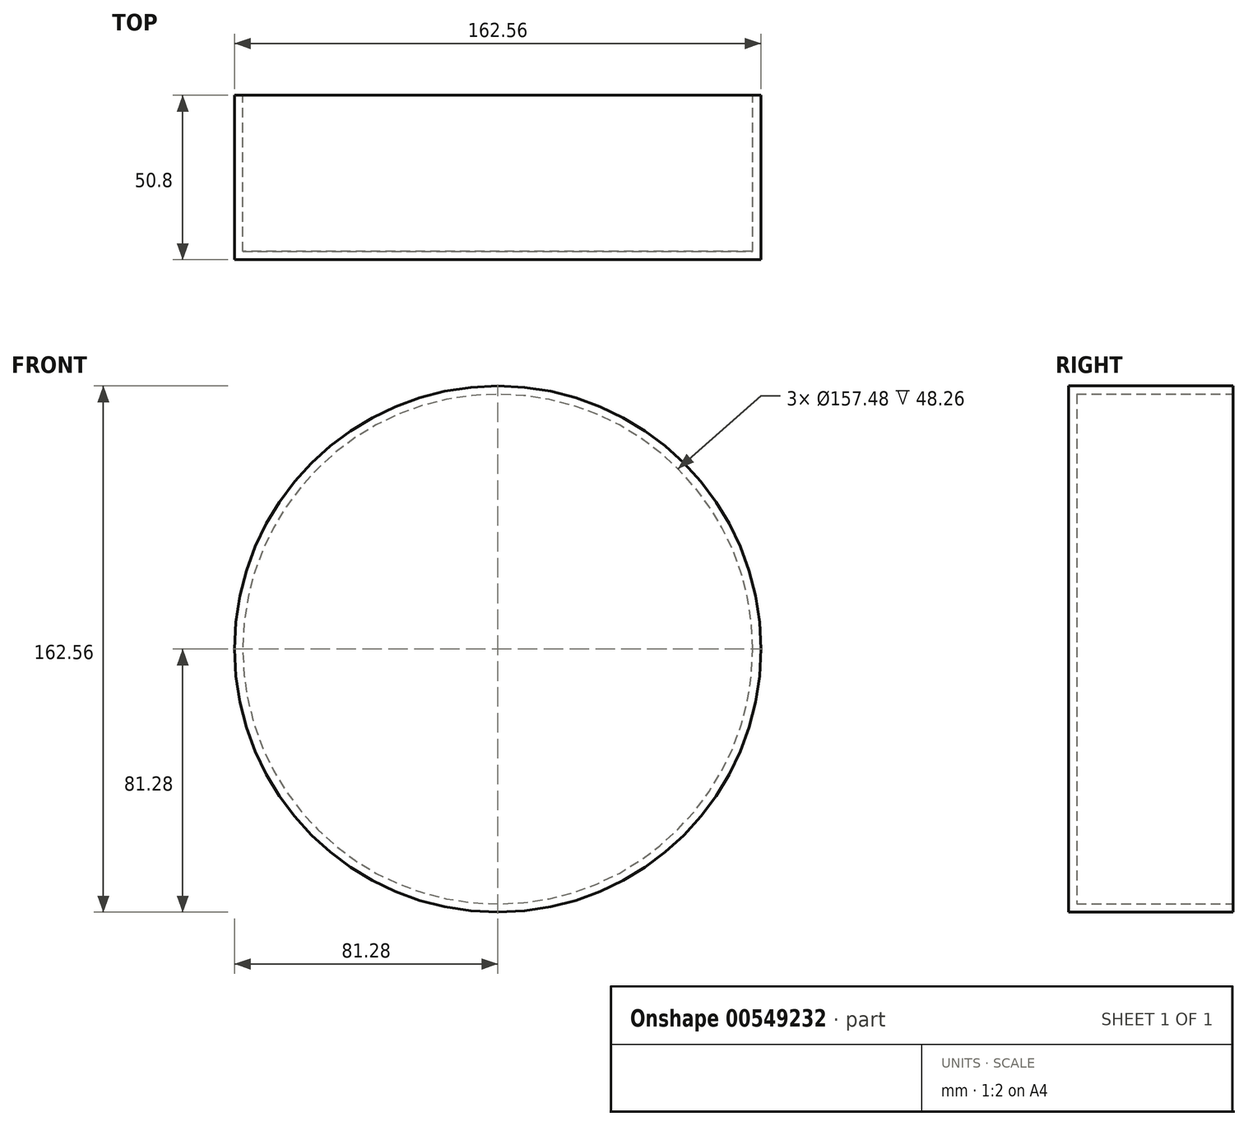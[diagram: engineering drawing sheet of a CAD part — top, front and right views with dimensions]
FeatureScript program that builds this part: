
annotation { "Feature Type Name" : "Feature", "Feature Type Description" : "" }
export const myFeature = defineFeature(function(context is Context, id is Id, definition is map)
    precondition{}
    {
        {
            var Q0;
            Q0=qCreatedBy(makeId("Top.planeOp"),FACE);
            var sketch = newSketch(context, id + "F0", { "sketchPlane" : qUnion([Q0])});
            skLineSegment(sketch, "E0.bottom", {"start": v(0, 0) * mm, "end": v(-81.28, 0) * mm});
            skLineSegment(sketch, "E0.top", {"start": v(0, 2.54) * mm, "end": v(-78.74, 2.54) * mm});
            skLineSegment(sketch, "E0.left", {"start": v(0, 0) * mm, "end": v(0, 2.54) * mm});
            skLineSegment(sketch, "E0.right", {"start": v(-81.28, 0) * mm, "end": v(-81.28, 50.8) * mm});
            skLineSegment(sketch, "E1", {"start": v(-78.74, 2.54) * mm, "end": v(-78.74, 50.8) * mm});
            skLineSegment(sketch, "E2", {"start": v(-78.74, 50.8) * mm, "end": v(-81.28, 50.8) * mm});
            skLineSegment(sketch, "E3", {"start": v(0, 30.4) * mm, "end": v(0, -8.9) * mm, "construction": true});
            skSolve(sketch);
        }
        {
            var Q0;
            Q0=makeQuery(id+"F0.imprint","IMPRINT",FACE,{"disambiguationData":[TD([[makeQuery(id+"F0.imprint","IMPRINT",EDGE,{"derivedFrom":sQuery(id+"F0.wireOp",EDGE,"E0.bottom")}),-1.0]])]});
            var Q1;
            Q1=sQuery(id+"F0.wireOp",EDGE,"E3");
            revolve(context, id + "F1", {"entities" : qUnion([Q0]), "axis" : qUnion([Q1]), "revolveType" : RevolveType.FULL});
        }
    });
